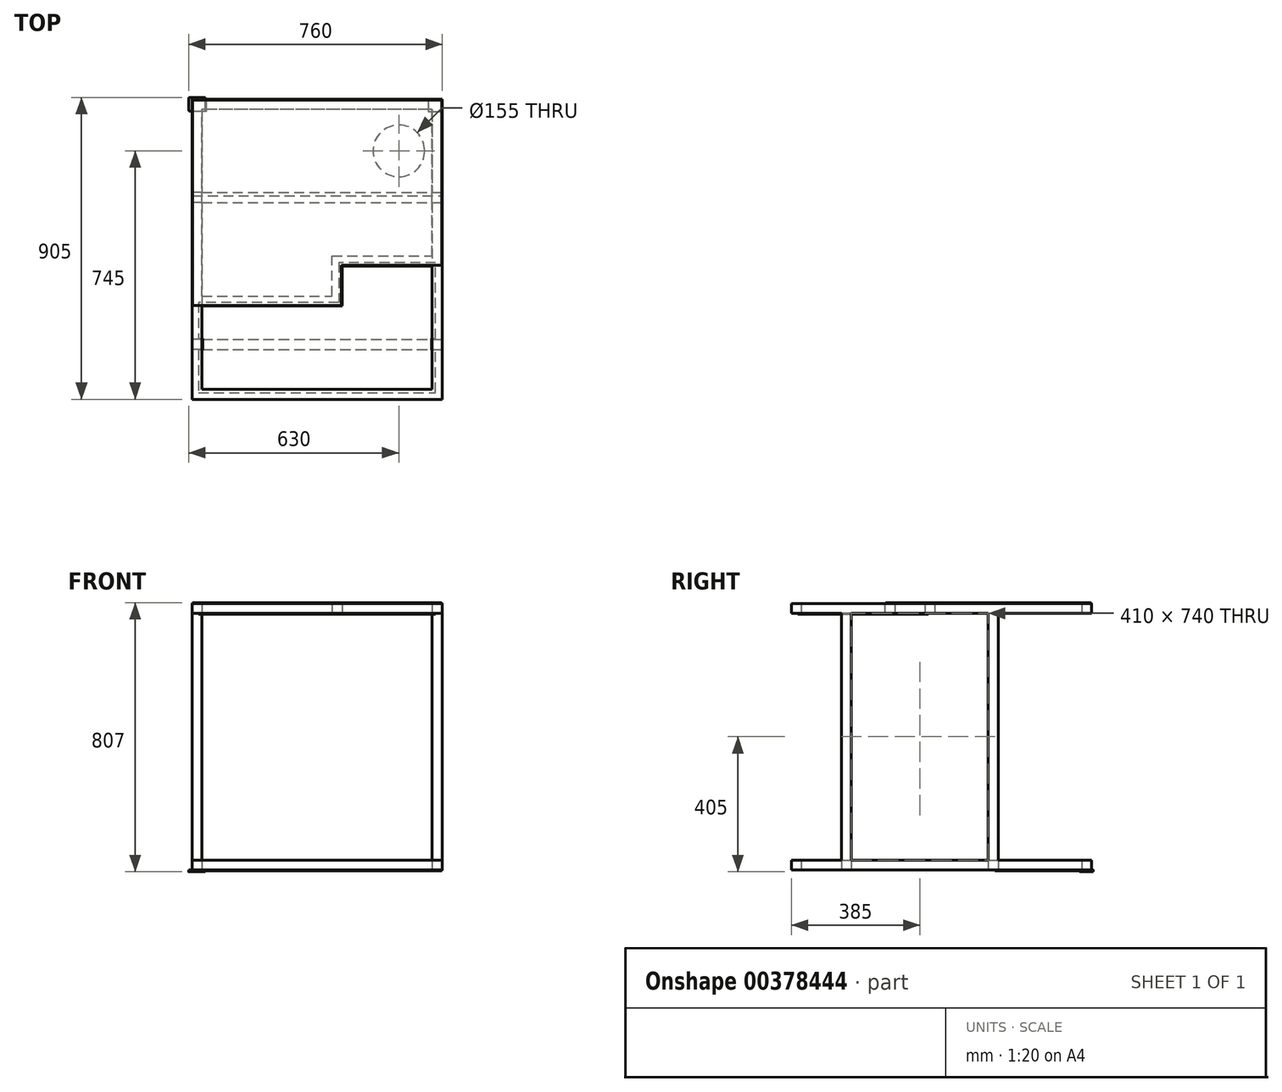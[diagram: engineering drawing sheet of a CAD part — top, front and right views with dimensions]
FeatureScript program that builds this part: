
annotation { "Feature Type Name" : "Feature", "Feature Type Description" : "" }
export const myFeature = defineFeature(function(context is Context, id is Id, definition is map)
    precondition{}
    {
        {
            var Q0;
            Q0=qCreatedBy(makeId("Top.planeOp"),FACE);
            var sketch = newSketch(context, id + "F0", { "sketchPlane" : qUnion([Q0])});
            skLineSegment(sketch, "E0.bottom", {"start": v(375, 450) * mm, "end": v(-375, 450) * mm});
            skLineSegment(sketch, "E0.top", {"start": v(375, -450) * mm, "end": v(-375, -450) * mm});
            skLineSegment(sketch, "E0.left", {"start": v(375, 450) * mm, "end": v(375, -450) * mm});
            skLineSegment(sketch, "E0.right", {"start": v(-375, 450) * mm, "end": v(-375, -450) * mm});
            skPoint(sketch, "E0.middle", {"position": v(0, 0) * mm});
            skLineSegment(sketch, "E1.bottom", {"start": v(345, 420) * mm, "end": v(-345, 420) * mm});
            skLineSegment(sketch, "E1.top", {"start": v(345, -420) * mm, "end": v(-345, -420) * mm});
            skLineSegment(sketch, "E1.left", {"start": v(345, 420) * mm, "end": v(345, 170) * mm});
            skLineSegment(sketch, "E1.right", {"start": v(-345, 420) * mm, "end": v(-345, 170) * mm});
            skLineSegment(sketch, "E2", {"start": v(-345, 170) * mm, "end": v(345, 170) * mm});
            skLineSegment(sketch, "E3", {"start": v(-345, 140) * mm, "end": v(345, 140) * mm});
            skLineSegment(sketch, "E4", {"start": v(-345, -300) * mm, "end": v(345, -300) * mm});
            skLineSegment(sketch, "E5", {"start": v(-345, -270) * mm, "end": v(345, -270) * mm});
            skLineSegment(sketch, "E6.trimOffspring", {"start": v(345, -300) * mm, "end": v(345, -420) * mm});
            skLineSegment(sketch, "E7.trimOffspring", {"start": v(-345, -300) * mm, "end": v(-345, -420) * mm});
            skLineSegment(sketch, "E8.trimOffspring", {"start": v(-345, 140) * mm, "end": v(-345, -270) * mm});
            skLineSegment(sketch, "E9.trimOffspring", {"start": v(345, 140) * mm, "end": v(345, -270) * mm});
            skSolve(sketch);
        }
        {
            var Q0;
            Q0=makeQuery(id+"F0.imprint","IMPRINT",FACE,{"disambiguationData":[TD([[makeQuery(id+"F0.imprint","IMPRINT",EDGE,{"derivedFrom":sQuery(id+"F0.wireOp",EDGE,"E0.bottom")}),1.0]])]});
            extrude(context, id + "F1", {"entities" : qUnion([Q0]), "depth" : 30 * mm});
        }
        {
            var Q0;
            Q0=makeQuery(id+"F1.opExtrude","CAP_FACE",FACE,{"disambiguationData":[OSD([sQuery(id+"F0.wireOp",EDGE,"E0.bottom"),sQuery(id+"F0.wireOp",EDGE,"E0.top"),sQuery(id+"F0.wireOp",EDGE,"E0.left"),sQuery(id+"F0.wireOp",EDGE,"E0.right"),sQuery(id+"F0.wireOp",EDGE,"E1.bottom"),sQuery(id+"F0.wireOp",EDGE,"E1.top"),sQuery(id+"F0.wireOp",EDGE,"E1.left"),sQuery(id+"F0.wireOp",EDGE,"E1.right"),sQuery(id+"F0.wireOp",EDGE,"E2"),sQuery(id+"F0.wireOp",EDGE,"E3"),sQuery(id+"F0.wireOp",EDGE,"E4"),sQuery(id+"F0.wireOp",EDGE,"E5"),sQuery(id+"F0.wireOp",EDGE,"E6.trimOffspring"),sQuery(id+"F0.wireOp",EDGE,"E7.trimOffspring"),sQuery(id+"F0.wireOp",EDGE,"E8.trimOffspring"),sQuery(id+"F0.wireOp",EDGE,"E9.trimOffspring")])],"isStart":false});
            var sketch = newSketch(context, id + "F2", { "sketchPlane" : qUnion([Q0])});
            skLineSegment(sketch, "E10.bottom", {"start": v(-345, 140) * mm, "end": v(-375, 140) * mm});
            skLineSegment(sketch, "E10.top", {"start": v(-345, 170) * mm, "end": v(-375, 170) * mm});
            skLineSegment(sketch, "E10.left", {"start": v(-345, 140) * mm, "end": v(-345, 170) * mm});
            skLineSegment(sketch, "E10.right", {"start": v(-375, 140) * mm, "end": v(-375, 170) * mm});
            skLineSegment(sketch, "E11.bottom", {"start": v(345, 140) * mm, "end": v(375, 140) * mm});
            skLineSegment(sketch, "E11.top", {"start": v(345, 170) * mm, "end": v(375, 170) * mm});
            skLineSegment(sketch, "E11.left", {"start": v(345, 140) * mm, "end": v(345, 170) * mm});
            skLineSegment(sketch, "E11.right", {"start": v(375, 140) * mm, "end": v(375, 170) * mm});
            skLineSegment(sketch, "E12.bottom", {"start": v(-345, -300) * mm, "end": v(-375, -300) * mm});
            skLineSegment(sketch, "E12.top", {"start": v(-345, -270) * mm, "end": v(-375, -270) * mm});
            skLineSegment(sketch, "E12.left", {"start": v(-345, -300) * mm, "end": v(-345, -270) * mm});
            skLineSegment(sketch, "E12.right", {"start": v(-375, -300) * mm, "end": v(-375, -270) * mm});
            skLineSegment(sketch, "E13.bottom", {"start": v(345, -300) * mm, "end": v(375, -300) * mm});
            skLineSegment(sketch, "E13.top", {"start": v(345, -270) * mm, "end": v(375, -270) * mm});
            skLineSegment(sketch, "E13.left", {"start": v(345, -300) * mm, "end": v(345, -270) * mm});
            skLineSegment(sketch, "E13.right", {"start": v(375, -300) * mm, "end": v(375, -270) * mm});
            skSolve(sketch);
        }
        {
            var Q0;
            Q0=makeQuery(id+"F2.imprint","IMPRINT",FACE,{"disambiguationData":[TD([[makeQuery(id+"F2.imprint","IMPRINT",EDGE,{"derivedFrom":sQuery(id+"F2.wireOp",EDGE,"E12.bottom")}),-1.0]])]});
            var Q1;
            Q1=makeQuery(id+"F2.imprint","IMPRINT",FACE,{"disambiguationData":[TD([[makeQuery(id+"F2.imprint","IMPRINT",EDGE,{"derivedFrom":sQuery(id+"F2.wireOp",EDGE,"E13.bottom")}),1.0]])]});
            var Q2;
            Q2=makeQuery(id+"F2.imprint","IMPRINT",FACE,{"disambiguationData":[TD([[makeQuery(id+"F2.imprint","IMPRINT",EDGE,{"derivedFrom":sQuery(id+"F2.wireOp",EDGE,"E11.bottom")}),1.0]])]});
            var Q3;
            Q3=makeQuery(id+"F2.imprint","IMPRINT",FACE,{"disambiguationData":[TD([[makeQuery(id+"F2.imprint","IMPRINT",EDGE,{"derivedFrom":sQuery(id+"F2.wireOp",EDGE,"E10.bottom")}),-1.0]])]});
            extrude(context, id + "F3", {"entities" : qUnion([Q0, Q1, Q2, Q3]), "operationType" : NewBodyOperationType.ADD, "depth" : (800 - 60) * mm});
        }
        {
            var Q0;
            Q0=makeQuery(id+"F1.opExtrude","CAP_FACE",FACE,{"disambiguationData":[OSD([sQuery(id+"F0.wireOp",EDGE,"E0.bottom"),sQuery(id+"F0.wireOp",EDGE,"E0.top"),sQuery(id+"F0.wireOp",EDGE,"E0.left"),sQuery(id+"F0.wireOp",EDGE,"E0.right"),sQuery(id+"F0.wireOp",EDGE,"E1.bottom"),sQuery(id+"F0.wireOp",EDGE,"E1.top"),sQuery(id+"F0.wireOp",EDGE,"E1.left"),sQuery(id+"F0.wireOp",EDGE,"E1.right"),sQuery(id+"F0.wireOp",EDGE,"E2"),sQuery(id+"F0.wireOp",EDGE,"E3"),sQuery(id+"F0.wireOp",EDGE,"E4"),sQuery(id+"F0.wireOp",EDGE,"E5"),sQuery(id+"F0.wireOp",EDGE,"E6.trimOffspring"),sQuery(id+"F0.wireOp",EDGE,"E7.trimOffspring"),sQuery(id+"F0.wireOp",EDGE,"E8.trimOffspring"),sQuery(id+"F0.wireOp",EDGE,"E9.trimOffspring")])],"isStart":true});
            var sketch = newSketch(context, id + "F4", { "sketchPlane" : qUnion([Q0])});
            skLineSegment(sketch, "E14.bottom", {"start": v(-383, -415) * mm, "end": v(-337, -415) * mm});
            skLineSegment(sketch, "E14.top", {"start": v(-383, -455) * mm, "end": v(-337, -455) * mm});
            skLineSegment(sketch, "E14.left", {"start": v(-385, -417) * mm, "end": v(-385, -453) * mm});
            skLineSegment(sketch, "E14.right", {"start": v(-335, -417) * mm, "end": v(-335, -453) * mm});
            skPoint(sketch, "E15.visualSharp", {"position": v(-385, -415) * mm});
            skArc(sketch, "E15.filletArc", {"start": v(-383, -415) * mm, "mid": v(-384.41, -415.59) * mm, "end": v(-385, -417) * mm});
            skPoint(sketch, "E16.visualSharp", {"position": v(-335, -415) * mm});
            skArc(sketch, "E16.filletArc", {"start": v(-335, -417) * mm, "mid": v(-335.59, -415.59) * mm, "end": v(-337, -415) * mm});
            skPoint(sketch, "E17.visualSharp", {"position": v(-335, -455) * mm});
            skArc(sketch, "E17.filletArc", {"start": v(-337, -455) * mm, "mid": v(-335.59, -454.41) * mm, "end": v(-335, -453) * mm});
            skPoint(sketch, "E18.visualSharp", {"position": v(-385, -455) * mm});
            skArc(sketch, "E18.filletArc", {"start": v(-385, -453) * mm, "mid": v(-384.41, -454.41) * mm, "end": v(-383, -455) * mm});
            skSolve(sketch);
        }
        {
            var Q0;
            {var subQ0=makeQuery(id+"F1.opExtrude","CAP_EDGE",EDGE,{"disambiguationData":[OSD([sQuery(id+"F0.wireOp",EDGE,"E0.right")])],"isStart":true});var subQ3=sQuery(id+"F4.wireOp",EDGE,"E14.bottom");var subQ4=makeQuery(id+"F4.imprint","INTERSECT",VERTEX,{"derivedFrom":[subQ0,subQ3]});Q0=makeQuery(id+"F4.imprint","IMPRINT",FACE,{"disambiguationData":[TD([[makeQuery(id+"F4.imprint","IMPRINT",EDGE,{"disambiguationData":[TD([[subQ4,-1.0]])],"derivedFrom":subQ3}),-1.0]])]});}
            var Q1;
            Q1=makeQuery(id+"F4.imprint","IMPRINT",FACE,{"disambiguationData":[TD([[makeQuery(id+"F4.imprint","IMPRINT",EDGE,{"derivedFrom":sQuery(id+"F4.wireOp",EDGE,"E14.top")}),1.0]])]});
            var Q2;
            {var subQ5=sQuery(id+"F4.wireOp",EDGE,"E16.filletArc");Q2=makeQuery(id+"F4.imprint","IMPRINT",FACE,{"disambiguationData":[TD([[makeQuery(id+"F4.imprint","IMPRINT",EDGE,{"derivedFrom":subQ5}),1.0]])]});}
            extrude(context, id + "F5", {"entities" : qUnion([Q0, Q1, Q2]), "depth" : 5 * mm});
        }
        {
            var Q0;
            Q0=makeQuery(id+"F3.opExtrude","CAP_FACE",FACE,{"disambiguationData":[OSD([sQuery(id+"F2.wireOp",EDGE,"E11.bottom"),sQuery(id+"F2.wireOp",EDGE,"E11.top"),sQuery(id+"F2.wireOp",EDGE,"E11.left"),sQuery(id+"F2.wireOp",EDGE,"E11.right")])],"isStart":false});
            var sketch = newSketch(context, id + "F6", { "sketchPlane" : qUnion([Q0])});
            skLineSegment(sketch, "E19.bottom", {"start": v(375, 450) * mm, "end": v(-375, 450) * mm});
            skLineSegment(sketch, "E19.top", {"start": v(375, -450) * mm, "end": v(-375, -450) * mm});
            skLineSegment(sketch, "E19.left", {"start": v(375, 450) * mm, "end": v(375, -450) * mm});
            skLineSegment(sketch, "E19.right", {"start": v(-375, 450) * mm, "end": v(-375, -450) * mm});
            skPoint(sketch, "E19.middle", {"position": v(0, 0) * mm});
            skLineSegment(sketch, "E20.bottom", {"start": v(345, 420) * mm, "end": v(-345, 420) * mm});
            skLineSegment(sketch, "E20.top", {"start": v(345, -420) * mm, "end": v(-345, -420) * mm});
            skLineSegment(sketch, "E21.MirrorCS", {"start": v(75, -50) * mm, "end": v(345, -50) * mm});
            skLineSegment(sketch, "E22.MirrorCS", {"start": v(45, -20) * mm, "end": v(345, -20) * mm});
            skLineSegment(sketch, "E23.MirrorCS", {"start": v(45, -140) * mm, "end": v(45, -20) * mm});
            skLineSegment(sketch, "E24.MirrorCS", {"start": v(-345, -170) * mm, "end": v(75, -170) * mm});
            skLineSegment(sketch, "E25.MirrorCS", {"start": v(-345, -140) * mm, "end": v(45, -140) * mm});
            skLineSegment(sketch, "E26.MirrorCS", {"start": v(75, -170) * mm, "end": v(75, -50) * mm});
            skLineSegment(sketch, "E27.trimOffspring", {"start": v(345, -50) * mm, "end": v(345, -420) * mm});
            skLineSegment(sketch, "E28.trimOffspring", {"start": v(-345, -170) * mm, "end": v(-345, -420) * mm});
            skLineSegment(sketch, "E29", {"start": v(345, -20) * mm, "end": v(345, 420) * mm});
            skLineSegment(sketch, "E30", {"start": v(-345, -140) * mm, "end": v(-345, 420) * mm});
            skSolve(sketch);
        }
        {
            var Q0;
            {var subQ0=sQuery(id+"F6.wireOp",EDGE,"E19.bottom");Q0=makeQuery(id+"F6.imprint","IMPRINT",FACE,{"disambiguationData":[TD([[makeQuery(id+"F6.imprint","IMPRINT",EDGE,{"derivedFrom":subQ0}),1.0]])]});}
            var Q1;
            {var subQ1=makeQuery(id+"F3.opExtrude","CAP_EDGE",EDGE,{"disambiguationData":[OSD([sQuery(id+"F2.wireOp",EDGE,"E11.bottom")])],"isStart":false});Q1=makeQuery(id+"F6.imprint","IMPRINT",FACE,{"disambiguationData":[TD([[makeQuery(id+"F6.imprint","IMPRINT",EDGE,{"derivedFrom":subQ1}),1.0]])]});}
            extrude(context, id + "F7", {"entities" : qUnion([Q0, Q1]), "operationType" : NewBodyOperationType.ADD, "depth" : 30 * mm});
        }
        {
            var Q0;
            Q0=makeQuery(id+"F7.opExtrude","CAP_FACE",FACE,{"disambiguationData":[OSD([sQuery(id+"F2.wireOp",EDGE,"E11.left"),sQuery(id+"F6.wireOp",EDGE,"E19.bottom"),sQuery(id+"F6.wireOp",EDGE,"E19.top"),sQuery(id+"F6.wireOp",EDGE,"E19.left"),sQuery(id+"F6.wireOp",EDGE,"E19.right"),sQuery(id+"F6.wireOp",EDGE,"E20.bottom"),sQuery(id+"F6.wireOp",EDGE,"E20.top"),sQuery(id+"F6.wireOp",EDGE,"E20.left"),sQuery(id+"F6.wireOp",EDGE,"E20.right"),sQuery(id+"F6.wireOp",EDGE,"5xM8RSOk-tIBh-xFcv-6GDI-QStuJs8O1zLM"),sQuery(id+"F6.wireOp",EDGE,"uj10pLO7-cmGp-t1DM-qDHd-ErLH6MrTC8v1"),sQuery(id+"F6.wireOp",EDGE,"Doms71RO-zl0a-rwn5-4mGu-1SjAuJ7yyaNh"),sQuery(id+"F6.wireOp",EDGE,"XXwqv2S9-Q7We-8TxV-A2jC-mrTuxE76FT1u"),sQuery(id+"F6.wireOp",EDGE,"e678830b-7910-4f95-95cd-7274655c18d9.trimOffspring"),sQuery(id+"F6.wireOp",EDGE,"374bdc1e-37c5-4ad0-9ae2-38c3f561be23.trimOffspring"),sQuery(id+"F6.wireOp",EDGE,"8601dc09-5c55-4954-8bd8-cb0075ae2c19.trimOffspring"),sQuery(id+"F6.wireOp",EDGE,"3e873d9f-9290-41d0-8945-3af6d96d1b6c.trimOffspring"),sQuery(id+"F6.wireOp",EDGE,"58h10Bz5-f8bS-egMF-Bm2b-2KDSHW4PDFA3"),sQuery(id+"F6.wireOp",EDGE,"AplArVB6-acle-I1GO-dKG7-WsaQGvYtVYIs"),sQuery(id+"F6.wireOp",EDGE,"aSH03Fq2-9BkX-UeEu-9WQh-R9fQN0osRNtQ"),sQuery(id+"F6.wireOp",EDGE,"TKTcrNcQ-Al6w-1uc8-AAej-js9Hl8U2omQz"),sQuery(id+"F6.wireOp",EDGE,"b583b906-7666-4362-9d97-fa7d1945a1d2.trimOffspring")])],"isStart":false});
            var sketch = newSketch(context, id + "F8", { "sketchPlane" : qUnion([Q0])});
            skLineSegment(sketch, "E31", {"start": v(-373, 448) * mm, "end": v(-373, -168) * mm});
            skLineSegment(sketch, "E32", {"start": v(-373, -168) * mm, "end": v(73, -168) * mm});
            skLineSegment(sketch, "E33", {"start": v(73, -168) * mm, "end": v(73, -48) * mm});
            skLineSegment(sketch, "E34", {"start": v(73, -48) * mm, "end": v(373, -48) * mm});
            skLineSegment(sketch, "E35", {"start": v(373, -48) * mm, "end": v(373, 448) * mm});
            skLineSegment(sketch, "E36", {"start": v(373, 448) * mm, "end": v(-373, 448) * mm});
            skSolve(sketch);
        }
        {
            var Q0;
            Q0=makeQuery(id+"F8.imprint","IMPRINT",FACE,{"disambiguationData":[TD([[makeQuery(id+"F8.imprint","IMPRINT",EDGE,{"derivedFrom":sQuery(id+"F8.wireOp",EDGE,"E31")}),1.0]])]});
            var Q1;
            Q1=makeQuery(id+"F8.imprint","IMPRINT",FACE,{"disambiguationData":[TD([[makeQuery(id+"F8.imprint","IMPRINT",EDGE,{"derivedFrom":makeQuery(id+"F7.opExtrude","CAP_EDGE",EDGE,{"disambiguationData":[OSD([sQuery(id+"F6.wireOp",EDGE,"E20.bottom")])],"isStart":false})}),1.0]])]});
            extrude(context, id + "F9", {"entities" : qUnion([Q0, Q1]), "depth" : 2 * mm});
        }
        {
            var Q0;
            Q0=makeQuery(id+"F1.opExtrude","CAP_FACE",FACE,{"disambiguationData":[OSD([sQuery(id+"F0.wireOp",EDGE,"E0.bottom"),sQuery(id+"F0.wireOp",EDGE,"E0.top"),sQuery(id+"F0.wireOp",EDGE,"E0.left"),sQuery(id+"F0.wireOp",EDGE,"E0.right"),sQuery(id+"F0.wireOp",EDGE,"E1.bottom"),sQuery(id+"F0.wireOp",EDGE,"E1.top"),sQuery(id+"F0.wireOp",EDGE,"E1.left"),sQuery(id+"F0.wireOp",EDGE,"E1.right"),sQuery(id+"F0.wireOp",EDGE,"E2"),sQuery(id+"F0.wireOp",EDGE,"E3"),sQuery(id+"F0.wireOp",EDGE,"E4"),sQuery(id+"F0.wireOp",EDGE,"E5"),sQuery(id+"F0.wireOp",EDGE,"E6.trimOffspring"),sQuery(id+"F0.wireOp",EDGE,"E7.trimOffspring"),sQuery(id+"F0.wireOp",EDGE,"E8.trimOffspring"),sQuery(id+"F0.wireOp",EDGE,"E9.trimOffspring")])],"isStart":true});
            var sketch = newSketch(context, id + "F10", { "sketchPlane" : qUnion([Q0])});
            skLineSegment(sketch, "E37.bottom", {"start": v(0, -448) * mm, "end": v(-333, -448) * mm});
            skLineSegment(sketch, "E37.top", {"start": v(0, -160) * mm, "end": v(-373, -160) * mm});
            skLineSegment(sketch, "E37.right", {"start": v(-373, -413) * mm, "end": v(-373, -160) * mm});
            skPoint(sketch, "E37.middle", {"position": v(-186.5, -304) * mm});
            skLineSegment(sketch, "E38", {"start": v(0, 0) * mm, "end": v(0, -736.9) * mm, "construction": true});
            skLineSegment(sketch, "E39", {"start": v(-333, -448) * mm, "end": v(-333, -413) * mm});
            skLineSegment(sketch, "E40", {"start": v(-333, -413) * mm, "end": v(-373, -413) * mm});
            skPoint(sketch, "E41.orphan", {"position": v(-373, -448) * mm});
            skLineSegment(sketch, "E42.MirrorCS", {"start": v(333, -413) * mm, "end": v(373, -413) * mm});
            skLineSegment(sketch, "E43.MirrorCS", {"start": v(333, -448) * mm, "end": v(333, -413) * mm});
            skPoint(sketch, "E44.MirrorP", {"position": v(373, -448) * mm});
            skLineSegment(sketch, "E45.MirrorCS", {"start": v(0, -448) * mm, "end": v(333, -448) * mm});
            skLineSegment(sketch, "E46.MirrorCS", {"start": v(373, -413) * mm, "end": v(373, -160) * mm});
            skLineSegment(sketch, "E47.MirrorCS", {"start": v(0, -160) * mm, "end": v(373, -160) * mm});
            skPoint(sketch, "E48.MirrorP", {"position": v(186.5, -304) * mm});
            skCircle(sketch, "E49", {"center": v(245, -295) * mm, "radius": 77.5 * mm});
            skLineSegment(sketch, "E50", {"start": v(345, -295) * mm, "end": v(99.64, -295) * mm, "construction": true});
            skSolve(sketch);
        }
        {
            var Q0;
            Q0=makeQuery(id+"F10.imprint","IMPRINT",FACE,{"disambiguationData":[TD([[makeQuery(id+"F10.imprint","IMPRINT",EDGE,{"derivedFrom":sQuery(id+"F10.wireOp",EDGE,"E37.top")}),1.0]])]});
            var Q1;
            {var subQ13=makeQuery(id+"F1.opExtrude","CAP_EDGE",EDGE,{"disambiguationData":[OSD([sQuery(id+"F0.wireOp",EDGE,"E2")])],"isStart":true});Q1=makeQuery(id+"F10.imprint","IMPRINT",FACE,{"disambiguationData":[TD([[makeQuery(id+"F10.imprint","IMPRINT",EDGE,{"derivedFrom":subQ13}),-1.0]])]});}
            var Q2;
            {var subQ1=sQuery(id+"F10.wireOp",EDGE,"E37.bottom");Q2=makeQuery(id+"F10.imprint","IMPRINT",FACE,{"disambiguationData":[TD([[makeQuery(id+"F10.imprint","IMPRINT",EDGE,{"derivedFrom":subQ1}),-1.0]])]});}
            extrude(context, id + "F11", {"entities" : qUnion([Q0, Q1, Q2]), "operationType" : NewBodyOperationType.ADD, "depth" : 2 * mm});
        }
        {
            var Q0;
            {var subQ0=sQuery(id+"F6.wireOp",EDGE,"E20.bottom");var subQ1=sQuery(id+"F6.wireOp",EDGE,"E19.bottom");var subQ2=sQuery(id+"F2.wireOp",EDGE,"E11.left");var subQ3=sQuery(id+"F6.wireOp",EDGE,"E20.right");var subQ4=sQuery(id+"F6.wireOp",EDGE,"374bdc1e-37c5-4ad0-9ae2-38c3f561be23.trimOffspring");var subQ5=sQuery(id+"F6.wireOp",EDGE,"XXwqv2S9-Q7We-8TxV-A2jC-mrTuxE76FT1u");var subQ6=sQuery(id+"F6.wireOp",EDGE,"E20.left");var subQ7=sQuery(id+"F6.wireOp",EDGE,"E19.right");var subQ8=sQuery(id+"F6.wireOp",EDGE,"E19.left");var subQ9=makeQuery(id+"F7.opExtrude","CAP_FACE",FACE,{"disambiguationData":[OSD([subQ2,subQ1,sQuery(id+"F6.wireOp",EDGE,"E19.top"),subQ8,subQ7,subQ0,sQuery(id+"F6.wireOp",EDGE,"E20.top"),subQ6,subQ3,sQuery(id+"F6.wireOp",EDGE,"5xM8RSOk-tIBh-xFcv-6GDI-QStuJs8O1zLM"),sQuery(id+"F6.wireOp",EDGE,"uj10pLO7-cmGp-t1DM-qDHd-ErLH6MrTC8v1"),sQuery(id+"F6.wireOp",EDGE,"Doms71RO-zl0a-rwn5-4mGu-1SjAuJ7yyaNh"),subQ5,sQuery(id+"F6.wireOp",EDGE,"e678830b-7910-4f95-95cd-7274655c18d9.trimOffspring"),subQ4,sQuery(id+"F6.wireOp",EDGE,"8601dc09-5c55-4954-8bd8-cb0075ae2c19.trimOffspring"),sQuery(id+"F6.wireOp",EDGE,"3e873d9f-9290-41d0-8945-3af6d96d1b6c.trimOffspring"),sQuery(id+"F6.wireOp",EDGE,"58h10Bz5-f8bS-egMF-Bm2b-2KDSHW4PDFA3"),sQuery(id+"F6.wireOp",EDGE,"AplArVB6-acle-I1GO-dKG7-WsaQGvYtVYIs"),sQuery(id+"F6.wireOp",EDGE,"aSH03Fq2-9BkX-UeEu-9WQh-R9fQN0osRNtQ"),sQuery(id+"F6.wireOp",EDGE,"TKTcrNcQ-Al6w-1uc8-AAej-js9Hl8U2omQz"),sQuery(id+"F6.wireOp",EDGE,"b583b906-7666-4362-9d97-fa7d1945a1d2.trimOffspring")])],"isStart":true});Q0=makeQuery(id+"F7.boolean.opBoolean","SPLIT",FACE,{"disambiguationData":[TD([makeQuery(id+"F1.opExtrude","SWEPT_FACE",FACE,{"disambiguationData":[OSD([sQuery(id+"F0.wireOp",EDGE,"E0.left")])]}),makeQuery(id+"F1.opExtrude","SWEPT_FACE",FACE,{"disambiguationData":[OSD([sQuery(id+"F0.wireOp",EDGE,"E0.right")])]}),makeQuery(id+"F3.opExtrude","SWEPT_FACE",FACE,{"disambiguationData":[OSD([sQuery(id+"F2.wireOp",EDGE,"E10.top")])]}),makeQuery(id+"F3.opExtrude","SWEPT_FACE",FACE,{"disambiguationData":[OSD([sQuery(id+"F2.wireOp",EDGE,"E10.left")])]}),makeQuery(id+"F3.opExtrude","SWEPT_FACE",FACE,{"disambiguationData":[OSD([sQuery(id+"F2.wireOp",EDGE,"E10.right")])]}),makeQuery(id+"F3.opExtrude","SWEPT_FACE",FACE,{"disambiguationData":[OSD([sQuery(id+"F2.wireOp",EDGE,"E11.top")])]}),makeQuery(id+"F3.opExtrude","SWEPT_FACE",FACE,{"disambiguationData":[OSD([subQ2])]}),makeQuery(id+"F3.opExtrude","SWEPT_FACE",FACE,{"disambiguationData":[OSD([sQuery(id+"F2.wireOp",EDGE,"E11.right")])]}),makeQuery(id+"F3.opExtrude","SWEPT_FACE",FACE,{"disambiguationData":[OSD([sQuery(id+"F2.wireOp",EDGE,"E12.right")])]}),makeQuery(id+"F3.opExtrude","SWEPT_FACE",FACE,{"disambiguationData":[OSD([sQuery(id+"F2.wireOp",EDGE,"E13.right")])]}),makeQuery(id+"F7.opExtrude","SWEPT_FACE",FACE,{"disambiguationData":[OSD([subQ1])]}),subQ9,makeQuery(id+"F7.opExtrude","SWEPT_FACE",FACE,{"disambiguationData":[OSD([subQ8])]}),makeQuery(id+"F7.opExtrude","SWEPT_FACE",FACE,{"disambiguationData":[OSD([subQ7])]}),makeQuery(id+"F7.opExtrude","SWEPT_FACE",FACE,{"disambiguationData":[OSD([subQ0])]}),makeQuery(id+"F7.opExtrude","SWEPT_FACE",FACE,{"disambiguationData":[OSD([subQ2,subQ6,subQ4])]}),makeQuery(id+"F7.opExtrude","SWEPT_FACE",FACE,{"disambiguationData":[OSD([subQ3])]}),makeQuery(id+"F7.opExtrude","SWEPT_FACE",FACE,{"disambiguationData":[OSD([subQ5])]})])],"derivedFrom":subQ9});}
            var sketch = newSketch(context, id + "F12", { "sketchPlane" : qUnion([Q0])});
            skLineSegment(sketch, "E51", {"start": v(355, 430) * mm, "end": v(355, 302) * mm});
            skLineSegment(sketch, "E52", {"start": v(355, 302) * mm, "end": v(343, 302) * mm});
            skLineSegment(sketch, "E53", {"start": v(343, 302) * mm, "end": v(343, 268) * mm});
            skLineSegment(sketch, "E54", {"start": v(343, 268) * mm, "end": v(355, 268) * mm});
            skLineSegment(sketch, "E55", {"start": v(355, 268) * mm, "end": v(355, 40) * mm});
            skLineSegment(sketch, "E56", {"start": v(355, 40) * mm, "end": v(65, 40) * mm});
            skLineSegment(sketch, "E57", {"start": v(65, 40) * mm, "end": v(65, 160) * mm});
            skLineSegment(sketch, "E58", {"start": v(65, 160) * mm, "end": v(-355, 160) * mm});
            skLineSegment(sketch, "E59", {"start": v(-355, 160) * mm, "end": v(-355, 268) * mm});
            skLineSegment(sketch, "E60", {"start": v(-355, 268) * mm, "end": v(-343, 268) * mm});
            skLineSegment(sketch, "E61", {"start": v(-343, 268) * mm, "end": v(-343, 302) * mm});
            skLineSegment(sketch, "E62", {"start": v(-343, 302) * mm, "end": v(-355, 302) * mm});
            skLineSegment(sketch, "E63", {"start": v(-355, 302) * mm, "end": v(-355, 430) * mm});
            skLineSegment(sketch, "E64", {"start": v(-355, 430) * mm, "end": v(355, 430) * mm});
            skSolve(sketch);
        }
        {
            var Q0;
            Q0 = qSketchRegion(id + "F12", true);
            extrude(context, id + "F13", {"entities" : qUnion([Q0]), "depth" : 2 * mm});
        }
    });
